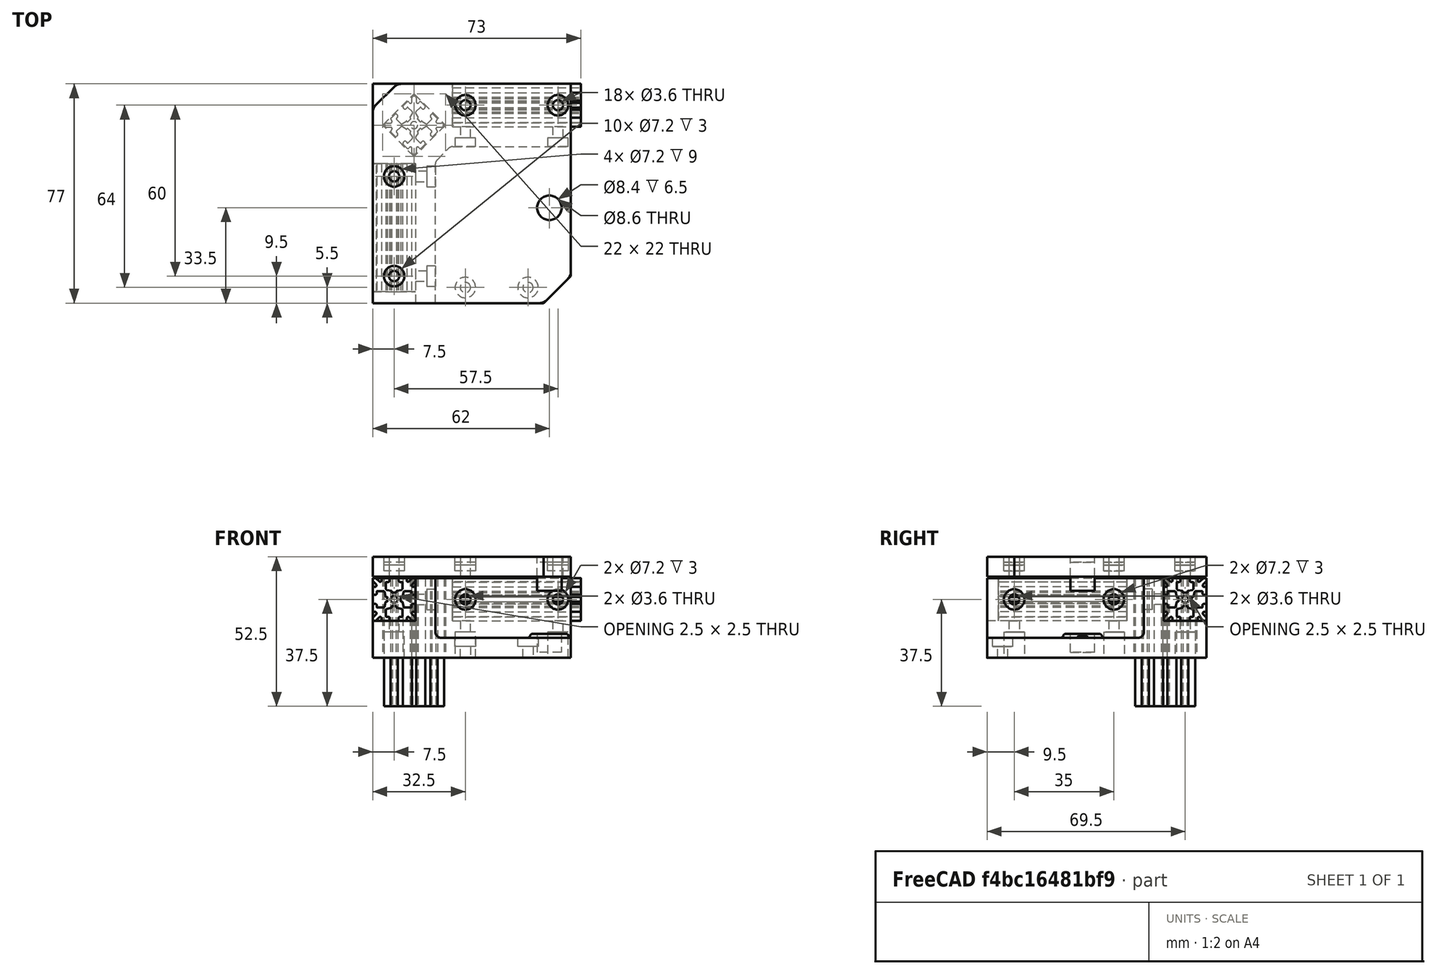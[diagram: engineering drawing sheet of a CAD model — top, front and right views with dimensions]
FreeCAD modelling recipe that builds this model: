
FCSTD DOCUMENT  (FreeCAD 0.15R4671 (Git))
Label: TopCornerCapIdler
License: All rights reserved
LicenseURL: http://en.wikipedia.org/wiki/All_rights_reserved
objects: Part::Feature×5, Sketcher::SketchObject×4, PartDesign::Pocket×3, Mesh::Feature×3, PartDesign::Fillet×2, PartDesign::Pad×1
note: 19 computed .brp shape members not serialized (recipe doc carries the construction recipe); baked Part::Feature solids carry a one-line shape summary decoded from their .brp

FEATURE [Sketcher::SketchObject] Sketch
  Placement = pos=(0,0,2) rot=(0,0,1;0rad)
  sketch-geometry (9):
    g0: LineSegment StartX=-7.5 StartY=7.5 StartZ=0 EndX=62.0538 EndY=7.5 EndZ=0
    g1: LineSegment StartX=62.0538 StartY=7.5 StartZ=0 EndX=62.0538 EndY=-59.9462 EndZ=0
    g2: LineSegment StartX=62.0538 StartY=-59.9462 StartZ=0 EndX=52.5 EndY=-69.5 EndZ=0
    g3: LineSegment StartX=52.5 StartY=-69.5 StartZ=0 EndX=-7.5 EndY=-69.5 EndZ=0
    g4: LineSegment StartX=-7.5 StartY=-69.5 StartZ=0 EndX=-7.5 EndY=7.5 EndZ=0
    g5: Circle CenterX=25 CenterY=0 CenterZ=0 NormalX=0 NormalY=0 NormalZ=1 Radius=1.8
    g6: Circle CenterX=57.5 CenterY=0 CenterZ=0 NormalX=0 NormalY=0 NormalZ=1 Radius=1.8
    g7: Circle CenterX=0 CenterY=-25 CenterZ=0 NormalX=0 NormalY=0 NormalZ=1 Radius=1.8
    g8: Circle CenterX=0 CenterY=-60 CenterZ=0 NormalX=0 NormalY=0 NormalZ=1 Radius=1.8
  constraints (16):
    c: Coincident(g0,g1)
    c: Coincident(g1,g2)
    c: Coincident(g2,g3)
    c: Coincident(g3,g4)
    c: Coincident(g4,g0)
    c: Horizontal(g3)
    c: Horizontal(g0)
    c: Vertical(g1)
    c: Vertical(g4)
    c: Angle(g2,g-2) = 0.785398
    c: DistanceX(g0) = -7.5
    c: DistanceY(g0) = 7.5
    c: Radius(g5) = 1.8
    c: Radius(g6) = 1.8
    c: Radius(g7) = 1.8
    c: Radius(g8) = 1.8
FEATURE [Part::Feature] Part__Feature  label="OB1515_45mm001"
  Placement = pos=(0,-20.5,-6) rot=(1,0,0;1.5708rad)
  shape: bbox 15 x 45 x 15 mm, 158 faces (baked)
FEATURE [Part::Feature] Part__Feature001  label="OB1515_45mm002"
  Placement = pos=(20.5,0,-6) rot=(0.57735,0.57735,0.57735;2.0944rad)
  shape: bbox 45 x 15 x 15 mm, 158 faces (baked)
FEATURE [Part::Feature] Part__Feature002  label="OB1515_45mm"
  Placement = pos=(7,-7,-43.5) rot=(0,0,1;0.785398rad)
  shape: bbox 21.01 x 21.01 x 45 mm, 158 faces (baked)
FEATURE [PartDesign::Pad] Pad
  Length = 7
  Length2 = 100
  Placement = pos=(0,0,2) rot=(0,0,1;0rad)
  Sketch = -> Sketch
  Type = 0
FEATURE [Sketcher::SketchObject] Sketch001
  Placement = pos=(0,0,9) rot=(0,0,1;0rad)
  Support = -> Pad [Face11]
  sketch-geometry (4):
    g0: Circle CenterX=57.5 CenterY=0 CenterZ=0 NormalX=0 NormalY=0 NormalZ=1 Radius=3.6
    g1: Circle CenterX=25 CenterY=0 CenterZ=0 NormalX=0 NormalY=0 NormalZ=1 Radius=3.6
    g2: Circle CenterX=0 CenterY=-25 CenterZ=0 NormalX=0 NormalY=0 NormalZ=1 Radius=3.6
    g3: Circle CenterX=0 CenterY=-60 CenterZ=0 NormalX=0 NormalY=0 NormalZ=1 Radius=3.6
  constraints (4):
    c: Radius(g0) = 3.6
    c: Radius(g1) = 3.6
    c: Radius(g2) = 3.6
    c: Radius(g3) = 3.6
FEATURE [PartDesign::Pocket] Pocket
  Length = 3
  Placement = pos=(0,0,2) rot=(0,0,1;0rad)
  Sketch = -> Sketch001
  Type = 0
FEATURE [Mesh::Feature] temp
FEATURE [Sketcher::SketchObject] Sketch002
  Placement = pos=(0,0,9) rot=(0,0,1;0rad)
  Support = -> Pocket [Face5]
  sketch-geometry (5):
    g0: LineSegment StartX=-8.5 StartY=-1 StartZ=0 EndX=-7.5 EndY=-1 EndZ=0
    g1: LineSegment StartX=-7.5 StartY=-1 StartZ=0 EndX=1 EndY=7.5 EndZ=0
    g2: LineSegment StartX=1 StartY=7.5 StartZ=0 EndX=1 EndY=8.5 EndZ=0
    g3: LineSegment StartX=1 StartY=8.5 StartZ=0 EndX=-8.5 EndY=8.5 EndZ=0
    g4: LineSegment StartX=-8.5 StartY=8.5 StartZ=0 EndX=-8.5 EndY=-1 EndZ=0
  constraints (5):
    c: Coincident(g0,g1)
    c: Coincident(g1,g2)
    c: Coincident(g2,g3)
    c: Coincident(g3,g4)
    c: Coincident(g4,g0)
FEATURE [PartDesign::Pocket] Pocket001
  Length = 5
  Placement = pos=(0,0,2) rot=(0,0,1;0rad)
  Sketch = -> Sketch002
  Type = 1
FEATURE [PartDesign::Fillet] Fillet
  Base = -> Pocket001 [Edge4,Edge24]
  Placement = pos=(0,0,2) rot=(0,0,1;0rad)
  Radius = 4
FEATURE [PartDesign::Fillet] Fillet001
  Base = -> Fillet [Edge30,Edge18]
  Placement = pos=(0,0,2) rot=(0,0,1;0rad)
  Radius = 4
FEATURE [Part::Feature] Part__Feature003  label="TopCornerIdler"
  Placement = pos=(0,0,-28.5) rot=(0,0,1;0rad)
  shape: bbox 70.18 x 77 x 28 mm, 72 faces (baked)
FEATURE [Mesh::Feature] _08ZZ_Ball_Bearing  label="608ZZ_Ball_Bearing"
  Placement = pos=(54.5,-36,-14.5) rot=(0,0,1;0rad)
FEATURE [Mesh::Feature] _08ZZ_Ball_Bearing001  label="608ZZ_Ball_Bearing001"
  Placement = pos=(54.5,-36,-3.4) rot=(0,0,1;0rad)
FEATURE [Sketcher::SketchObject] Sketch003
  Placement = pos=(0,0,9) rot=(0,0,1;0rad)
  Support = -> Fillet001 [Face16]
  sketch-geometry (1):
    g0: Circle CenterX=54.5 CenterY=-36 CenterZ=0 NormalX=0 NormalY=0 NormalZ=1 Radius=4.3
  constraints (1):
    c: Radius(g0) = 4.3
FEATURE [PartDesign::Pocket] Pocket002
  Length = 10
  Placement = pos=(0,0,2) rot=(0,0,1;0rad)
  Sketch = -> Sketch003
  Type = 0
FEATURE [Part::Feature] Pocket003
  shape: bbox 69.55 x 77 x 7 mm, 25 faces (baked)
